# Revit family: CA-4_DWDI_ARR_3_CW_UBD
name_source: partatom
category: Mechanical Equipment
units: mm (PartAtom-declared; Revit-internal decimal feet)

## family parameters
Always vertical = Yes
Cut with Voids When Loaded = No
Part Type = Normal
Room Calculation Point = No
Round Connector Dimension = Use Radius
Shared = No
Work Plane-Based = No

## types (54) — shared parameters
0 = 0"
1" = 1"
1.5 = 1 1/2"
2" = 2"
2' = 24"
3" = 3"
4" = 4"
Manufacturer = Loren Cook Company
ONE EIGTH = 1/8"
Type Comments = Airfoil Centrifugal Blower Arrangement 3 Clockwise Up Blast Discharge
URL = www.lorencook.com

## per-type parameters (varying)
- 120_CA-4_DWDI_ARR_3_CW_UBD_CLASS_1: (B/2)+.125"=8 31/32"; (B/2)+J=10 27/32"; (F/2)-S=3 7/8"; -(B/2)-J=-10 27/32"; -A=-12 1/8"; -B=-17 11/16"; -B/2=-8 27/32"; -J*1.5=-3"; -L+M=-22 15/16"; A=12 1/8"; A+.25"=12 3/8"; B=17 11/16"; B+.25"=17 15/16"; B/2=8 27/32"; D=25 15/16"; D/2=12 31/32"; D/8=3 1/4"; E=10 3/4"; EE=10 3/4"; F=22 3/4"; F-G=12 3/8"; F/2=11 3/8"; G=10 3/8"; G+(INLET_RAD+1.5")=20"; G+N=11 13/16"; G-(INLET_RAD+1.5")=3/4"; H=2"; INLET_DIA=16 1/4"; INLET_RAD=8 1/8"; INLET_RAD+1.5"=9 5/8"; INLET_RAD/2=4 1/16"; J=2"; J*1.5=3"; J-.125"=1 7/8"; L=28 11/16"; M=5 3/4"; Model=CA-4 DWDI CW UBD Class 1; N=1 7/16"; N*2=2 7/8"; N+A+H=15 9/16"; N/2=23/32"; O=9 31/32"; P=19 15/16"; P/2=9 31/32"; S=7 1/2"; T=11/16"; T/2=11/32"
- 120_CA-4_DWDI_ARR_3_CW_UBD_CLASS_2: (B/2)+.125"=8 31/32"; (B/2)+J=10 27/32"; (F/2)-S=3 7/8"; -(B/2)-J=-10 27/32"; -A=-12 1/8"; -B=-17 11/16"; -B/2=-8 27/32"; -J*1.5=-3"; -L+M=-23 5/16"; A=12 1/8"; A+.25"=12 3/8"; B=17 11/16"; B+.25"=17 15/16"; B/2=8 27/32"; D=25 15/16"; D/2=12 31/32"; D/8=3 1/4"; E=10 3/4"; EE=10 3/4"; F=22 3/4"; F-G=12 3/8"; F/2=11 3/8"; G=10 3/8"; G+(INLET_RAD+1.5")=20"; G+N=12 1/16"; G-(INLET_RAD+1.5")=3/4"; H=2"; INLET_DIA=16 1/4"; INLET_RAD=8 1/8"; INLET_RAD+1.5"=9 5/8"; INLET_RAD/2=4 1/16"; J=2"; J*1.5=3"; J-.125"=1 7/8"; L=29 7/16"; M=6 1/8"; Model=CA-4 DWDI CW UBD Class 2; N=1 11/16"; N*2=3 3/8"; N+A+H=15 13/16"; N/2=27/32"; O=9 31/32"; P=19 15/16"; P/2=9 31/32"; S=7 1/2"; T=11/16"; T/2=11/32"
- 120_CA-4_DWDI_ARR_3_CW_UBD_CLASS_3: (B/2)+.125"=8 31/32"; (B/2)+J=10 27/32"; (F/2)-S=3 7/8"; -(B/2)-J=-10 27/32"; -A=-12 1/8"; -B=-17 11/16"; -B/2=-8 27/32"; -J*1.5=-3"; -L+M=-23 9/16"; A=12 1/8"; A+.25"=12 3/8"; B=17 11/16"; B+.25"=17 15/16"; B/2=8 27/32"; D=25 15/16"; D/2=12 31/32"; D/8=3 1/4"; E=10 3/4"; EE=10 3/4"; F=22 3/4"; F-G=12 3/8"; F/2=11 3/8"; G=10 3/8"; G+(INLET_RAD+1.5")=20"; G+N=12 5/16"; G-(INLET_RAD+1.5")=3/4"; H=2"; INLET_DIA=16 1/4"; INLET_RAD=8 1/8"; INLET_RAD+1.5"=9 5/8"; INLET_RAD/2=4 1/16"; J=2"; J*1.5=3"; J-.125"=1 7/8"; L=29 15/16"; M=6 3/8"; Model=CA-4 DWDI CW UBD Class 3; N=1 15/16"; N*2=3 7/8"; N+A+H=16 1/16"; N/2=31/32"; O=9 31/32"; P=19 15/16"; P/2=9 31/32"; S=7 1/2"; T=11/16"; T/2=11/32"
- 135_CA-4_DWDI_ARR_3_CW_UBD_CLASS_1: (B/2)+.125"=10 3/32"; (B/2)+J=11 31/32"; (F/2)-S=4 1/4"; -(B/2)-J=-11 31/32"; -A=-13 5/8"; -B=-19 15/16"; -B/2=-9 31/32"; -J*1.5=-3"; -L+M=-25 3/16"; A=13 5/8"; A+.25"=13 7/8"; B=19 15/16"; B+.25"=20 3/16"; B/2=9 31/32"; D=25 1/2"; D/2=12 3/4"; D/8=3 3/16"; E=12"; EE=12"; F=25 1/2"; F-G=13 7/8"; F/2=12 3/4"; G=11 5/8"; G+(INLET_RAD+1.5")=22"; G+N=13 1/16"; G-(INLET_RAD+1.5")=1 1/4"; H=2"; INLET_DIA=17 3/4"; INLET_RAD=8 7/8"; INLET_RAD+1.5"=10 3/8"; INLET_RAD/2=4 7/16"; J=2"; J*1.5=3"; J-.125"=1 7/8"; L=30 15/16"; M=5 3/4"; Model=CA-4 DWDI CW UBD Class 1; N=1 7/16"; N*2=2 7/8"; N+A+H=17 1/16"; N/2=23/32"; O=11 3/32"; P=22 3/16"; P/2=11 3/32"; S=8 1/2"; T=11/16"; T/2=11/32"
- 135_CA-4_DWDI_ARR_3_CW_UBD_CLASS_2: (B/2)+.125"=10 3/32"; (B/2)+J=11 31/32"; (F/2)-S=4 1/4"; -(B/2)-J=-11 31/32"; -A=-13 5/8"; -B=-19 15/16"; -B/2=-9 31/32"; -J*1.5=-3"; -L+M=-25 9/16"; A=13 5/8"; A+.25"=13 7/8"; B=19 15/16"; B+.25"=20 3/16"; B/2=9 31/32"; D=28 13/16"; D/2=14 13/32"; D/8=3 19/32"; E=12"; EE=12"; F=25 1/2"; F-G=13 7/8"; F/2=12 3/4"; G=11 5/8"; G+(INLET_RAD+1.5")=22"; G+N=13 5/16"; G-(INLET_RAD+1.5")=1 1/4"; H=2"; INLET_DIA=17 3/4"; INLET_RAD=8 7/8"; INLET_RAD+1.5"=10 3/8"; INLET_RAD/2=4 7/16"; J=2"; J*1.5=3"; J-.125"=1 7/8"; L=31 11/16"; M=6 1/8"; Model=CA-4 DWDI CW UBD Class 2; N=1 11/16"; N*2=3 3/8"; N+A+H=17 5/16"; N/2=27/32"; O=11 3/32"; P=22 3/16"; P/2=11 3/32"; S=8 1/2"; T=11/16"; T/2=11/32"
- 135_CA-4_DWDI_ARR_3_CW_UBD_CLASS_3: (B/2)+.125"=10 3/32"; (B/2)+J=11 31/32"; (F/2)-S=4 1/4"; -(B/2)-J=-11 31/32"; -A=-13 5/8"; -B=-19 15/16"; -B/2=-9 31/32"; -J*1.5=-3"; -L+M=-26 1/16"; A=13 5/8"; A+.25"=13 7/8"; B=19 15/16"; B+.25"=20 3/16"; B/2=9 31/32"; D=28 13/16"; D/2=14 13/32"; D/8=3 19/32"; E=12"; EE=12"; F=25 1/2"; F-G=13 7/8"; F/2=12 3/4"; G=11 5/8"; G+(INLET_RAD+1.5")=22"; G+N=13 13/16"; G-(INLET_RAD+1.5")=1 1/4"; H=2"; INLET_DIA=17 3/4"; INLET_RAD=8 7/8"; INLET_RAD+1.5"=10 3/8"; INLET_RAD/2=4 7/16"; J=2"; J*1.5=3"; J-.125"=1 7/8"; L=32 11/16"; M=6 5/8"; Model=CA-4 DWDI CW UBD Class 3; N=2 3/16"; N*2=4 3/8"; N+A+H=17 13/16"; N/2=1 3/32"; O=11 3/32"; P=22 3/16"; P/2=11 3/32"; S=8 1/2"; T=11/16"; T/2=11/32"
- 150_CA-4_DWDI_ARR_3_CW_UBD_CLASS_1: (B/2)+.125"=11 1/8"; (B/2)+J=13"; (F/2)-S=5 1/16"; -(B/2)-J=-13"; -A=-15 1/4"; -B=-22"; -B/2=-11"; -J*1.5=-3"; -L+M=-27 5/8"; A=15 1/4"; A+.25"=15 1/2"; B=22"; B+.25"=22 1/4"; B/2=11"; D=31 11/16"; D/2=15 27/32"; D/8=3 31/32"; E=13 1/4"; EE=13 1/4"; F=28 1/8"; F-G=15 1/4"; F/2=14 1/16"; G=12 7/8"; G+(INLET_RAD+1.5")=24"; G+N=14 9/16"; G-(INLET_RAD+1.5")=1 3/4"; H=2"; INLET_DIA=19 1/4"; INLET_RAD=9 5/8"; INLET_RAD+1.5"=11 1/8"; INLET_RAD/2=4 13/16"; J=2"; J*1.5=3"; J-.125"=1 7/8"; L=34 1/4"; M=6 5/8"; Model=CA-4 DWDI CW UBD Class 1; N=1 11/16"; N*2=3 3/8"; N+A+H=18 15/16"; N/2=27/32"; O=12 1/8"; P=24 1/4"; P/2=12 1/8"; S=9"; T=11/16"; T/2=11/32"
- 150_CA-4_DWDI_ARR_3_CW_UBD_CLASS_2: (B/2)+.125"=11 1/8"; (B/2)+J=13"; (F/2)-S=5 1/16"; -(B/2)-J=-13"; -A=-15 1/4"; -B=-22"; -B/2=-11"; -J*1.5=-3"; -L+M=-27 7/8"; A=15 1/4"; A+.25"=15 1/2"; B=22"; B+.25"=22 1/4"; B/2=11"; D=31 11/16"; D/2=15 27/32"; D/8=3 31/32"; E=13 1/4"; EE=13 1/4"; F=28 1/8"; F-G=15 1/4"; F/2=14 1/16"; G=12 7/8"; G+(INLET_RAD+1.5")=24"; G+N=14 13/16"; G-(INLET_RAD+1.5")=1 3/4"; H=2"; INLET_DIA=19 1/4"; INLET_RAD=9 5/8"; INLET_RAD+1.5"=11 1/8"; INLET_RAD/2=4 13/16"; J=2"; J*1.5=3"; J-.125"=1 7/8"; L=34 3/4"; M=6 7/8"; Model=CA-4 DWDI CW UBD Class 2; N=1 15/16"; N*2=3 7/8"; N+A+H=19 3/16"; N/2=31/32"; O=12 1/8"; P=24 1/4"; P/2=12 1/8"; S=9"; T=11/16"; T/2=11/32"
- 150_CA-4_DWDI_ARR_3_CW_UBD_CLASS_3: (B/2)+.125"=11 1/8"; (B/2)+J=13"; (F/2)-S=5 1/16"; -(B/2)-J=-13"; -A=-15 1/4"; -B=-22"; -B/2=-11"; -J*1.5=-3"; -L+M=-28 1/4"; A=15 1/4"; A+.25"=15 1/2"; B=22"; B+.25"=22 1/4"; B/2=11"; D=31 11/16"; D/2=15 27/32"; D/8=3 31/32"; E=13 1/4"; EE=13 1/4"; F=28 1/8"; F-G=15 1/4"; F/2=14 1/16"; G=12 7/8"; G+(INLET_RAD+1.5")=24"; G+N=15 5/16"; G-(INLET_RAD+1.5")=1 3/4"; H=2"; INLET_DIA=19 1/4"; INLET_RAD=9 5/8"; INLET_RAD+1.5"=11 1/8"; INLET_RAD/2=4 13/16"; J=2"; J*1.5=3"; J-.125"=1 7/8"; L=35 1/2"; M=7 1/4"; Model=CA-4 DWDI CW UBD Class 3; N=2 7/16"; N*2=4 7/8"; N+A+H=19 11/16"; N/2=1 7/32"; O=12 1/8"; P=24 1/4"; P/2=12 1/8"; S=9"; T=11/16"; T/2=11/32"
- 165_CA-4_DWDI_ARR_3_CW_UBD_CLASS_1: (B/2)+.125"=12 1/8"; (B/2)+J=14"; (F/2)-S=5 7/16"; -(B/2)-J=-14"; -A=-16 15/16"; -B=-24"; -B/2=-12"; -J*1.5=-3"; -L+M=-29 5/8"; A=16 15/16"; A+.25"=17 3/16"; B=24"; B+.25"=24 1/4"; B/2=12"; D=34 7/16"; D/2=17 7/32"; D/8=4 5/16"; E=14 3/8"; EE=14 3/8"; F=30 7/8"; F-G=16 5/8"; F/2=15 7/16"; G=14 1/4"; G+(INLET_RAD+1.5")=26 3/8"; G+N=15 15/16"; G-(INLET_RAD+1.5")=2 1/8"; H=2"; INLET_DIA=21 1/4"; INLET_RAD=10 5/8"; INLET_RAD+1.5"=12 1/8"; INLET_RAD/2=5 5/16"; J=2"; J*1.5=3"; J-.125"=1 7/8"; L=36 1/4"; M=6 5/8"; Model=CA-4 DWDI CW UBD Class 1; N=1 11/16"; N*2=3 3/8"; N+A+H=20 5/8"; N/2=27/32"; O=13 1/8"; P=26 1/4"; P/2=13 1/8"; S=10"; T=11/16"; T/2=11/32"
- 165_CA-4_DWDI_ARR_3_CW_UBD_CLASS_2: (B/2)+.125"=12 1/8"; (B/2)+J=14"; (F/2)-S=5 7/16"; -(B/2)-J=-14"; -A=-16 15/16"; -B=-24"; -B/2=-12"; -J*1.5=-3"; -L+M=-29 7/8"; A=16 15/16"; A+.25"=17 3/16"; B=24"; B+.25"=24 1/4"; B/2=12"; D=34 7/16"; D/2=17 7/32"; D/8=4 5/16"; E=14 3/8"; EE=14 3/8"; F=30 7/8"; F-G=16 5/8"; F/2=15 7/16"; G=14 1/4"; G+(INLET_RAD+1.5")=26 3/8"; G+N=16 3/16"; G-(INLET_RAD+1.5")=2 1/8"; H=2"; INLET_DIA=21 1/4"; INLET_RAD=10 5/8"; INLET_RAD+1.5"=12 1/8"; INLET_RAD/2=5 5/16"; J=2"; J*1.5=3"; J-.125"=1 7/8"; L=36 3/4"; M=6 7/8"; Model=CA-4 DWDI CW UBD Class 2; N=1 15/16"; N*2=3 7/8"; N+A+H=20 7/8"; N/2=31/32"; O=13 1/8"; P=26 1/4"; P/2=13 1/8"; S=10"; T=11/16"; T/2=11/32"
- 165_CA-4_DWDI_ARR_3_CW_UBD_CLASS_3: (B/2)+.125"=12 1/8"; (B/2)+J=14"; (F/2)-S=5 7/16"; -(B/2)-J=-14"; -A=-16 15/16"; -B=-24"; -B/2=-12"; -J*1.5=-3"; -L+M=-30 5/16"; A=16 15/16"; A+.25"=17 3/16"; B=24"; B+.25"=24 1/4"; B/2=12"; D=34 7/16"; D/2=17 7/32"; D/8=4 5/16"; E=14 3/8"; EE=14 3/8"; F=30 7/8"; F-G=16 5/8"; F/2=15 7/16"; G=14 1/4"; G+(INLET_RAD+1.5")=26 3/8"; G+N=16 11/16"; G-(INLET_RAD+1.5")=2 1/8"; H=2"; INLET_DIA=21 1/4"; INLET_RAD=10 5/8"; INLET_RAD+1.5"=12 1/8"; INLET_RAD/2=5 5/16"; J=2"; J*1.5=3"; J-.125"=1 7/8"; L=37 1/2"; M=7 3/16"; Model=CA-4 DWDI CW UBD Class 3; N=2 7/16"; N*2=4 7/8"; N+A+H=21 3/8"; N/2=1 7/32"; O=13 1/8"; P=26 1/4"; P/2=13 1/8"; S=10"; T=11/16"; T/2=11/32"
- 180_CA-4_DWDI_ARR_3_CW_UBD_CLASS_1: (B/2)+.125"=13 5/32"; (B/2)+J=15 1/32"; (F/2)-S=5 13/16"; -(B/2)-J=-15 1/32"; -A=-18 1/2"; -B=-26 1/16"; -B/2=-13 1/32"; -J*1.5=-3"; -L+M=-31 11/16"; A=18 1/2"; A+.25"=18 3/4"; B=26 1/16"; B+.25"=26 5/16"; B/2=13 1/32"; D=37 5/16"; D/2=18 21/32"; D/8=4 21/32"; E=15 5/8"; EE=15 5/8"; F=33 5/8"; F-G=18 1/8"; F/2=16 13/16"; G=15 1/2"; G+(INLET_RAD+1.5")=28 3/8"; G+N=17 3/16"; G-(INLET_RAD+1.5")=2 5/8"; H=2"; INLET_DIA=22 3/4"; INLET_RAD=11 3/8"; INLET_RAD+1.5"=12 7/8"; INLET_RAD/2=5 11/16"; J=2"; J*1.5=3"; J-.125"=1 7/8"; L=38 13/16"; M=7 1/8"; Model=CA-4 DWDI CW UBD Class 1; N=1 11/16"; N*2=3 3/8"; N+A+H=22 3/16"; N/2=27/32"; O=14 5/32"; P=28 5/16"; P/2=14 5/32"; S=11"; T=11/16"; T/2=11/32"
- 180_CA-4_DWDI_ARR_3_CW_UBD_CLASS_2: (B/2)+.125"=13 5/32"; (B/2)+J=15 1/32"; (F/2)-S=5 13/16"; -(B/2)-J=-15 1/32"; -A=-18 1/2"; -B=-26 1/16"; -B/2=-13 1/32"; -J*1.5=-3"; -L+M=-31 15/16"; A=18 1/2"; A+.25"=18 3/4"; B=26 1/16"; B+.25"=26 5/16"; B/2=13 1/32"; D=37 5/16"; D/2=18 21/32"; D/8=4 21/32"; E=15 5/8"; EE=15 5/8"; F=33 5/8"; F-G=18 1/8"; F/2=16 13/16"; G=15 1/2"; G+(INLET_RAD+1.5")=28 3/8"; G+N=17 7/16"; G-(INLET_RAD+1.5")=2 5/8"; H=2"; INLET_DIA=22 3/4"; INLET_RAD=11 3/8"; INLET_RAD+1.5"=12 7/8"; INLET_RAD/2=5 11/16"; J=2"; J*1.5=3"; J-.125"=1 7/8"; L=39 5/16"; M=7 3/8"; Model=CA-4 DWDI CW UBD Class 2; N=1 15/16"; N*2=3 7/8"; N+A+H=22 7/16"; N/2=31/32"; O=14 5/32"; P=28 5/16"; P/2=14 5/32"; S=11"; T=11/16"; T/2=11/32"
- 180_CA-4_DWDI_ARR_3_CW_UBD_CLASS_3: (B/2)+.125"=13 5/32"; (B/2)+J=15 1/32"; (F/2)-S=5 13/16"; -(B/2)-J=-15 1/32"; -A=-18 1/2"; -B=-26 1/16"; -B/2=-13 1/32"; -J*1.5=-3"; -L+M=-32 5/16"; A=18 1/2"; A+.25"=18 3/4"; B=26 1/16"; B+.25"=26 5/16"; B/2=13 1/32"; D=37 5/16"; D/2=18 21/32"; D/8=4 21/32"; E=15 5/8"; EE=15 5/8"; F=33 5/8"; F-G=18 1/8"; F/2=16 13/16"; G=15 1/2"; G+(INLET_RAD+1.5")=28 3/8"; G+N=17 15/16"; G-(INLET_RAD+1.5")=2 5/8"; H=2"; INLET_DIA=22 3/4"; INLET_RAD=11 3/8"; INLET_RAD+1.5"=12 7/8"; INLET_RAD/2=5 11/16"; J=2"; J*1.5=3"; J-.125"=1 7/8"; L=40 1/16"; M=7 3/4"; Model=CA-4 DWDI CW UBD Class 3; N=2 7/16"; N*2=4 7/8"; N+A+H=22 15/16"; N/2=1 7/32"; O=14 5/32"; P=28 5/16"; P/2=14 5/32"; S=11"; T=11/16"; T/2=11/32"
- 195_CA-4_DWDI_ARR_3_CW_UBD_CLASS_1: (B/2)+.125"=14 11/32"; (B/2)+J=16 7/32"; (F/2)-S=6 5/8"; -(B/2)-J=-16 7/32"; -A=-19 1/2"; -B=-28 7/16"; -B/2=-14 7/32"; -J*1.5=-3"; -L+M=-34 7/16"; A=19 1/2"; A+.25"=19 3/4"; B=28 7/16"; B+.25"=28 11/16"; B/2=14 7/32"; D=40 1/16"; D/2=20 1/32"; D/8=5"; E=16 3/4"; EE=16 3/4"; F=36 1/4"; F-G=19 1/2"; F/2=18 1/8"; G=16 3/4"; G+(INLET_RAD+1.5")=30 3/8"; G+N=18 11/16"; G-(INLET_RAD+1.5")=3 1/8"; H=2"; INLET_DIA=24 1/4"; INLET_RAD=12 1/8"; INLET_RAD+1.5"=13 5/8"; INLET_RAD/2=6 1/16"; J=2"; J*1.5=3"; J-.125"=1 7/8"; L=41 11/16"; M=7 1/4"; Model=CA-4 DWDI CW UBD Class 1; N=1 15/16"; N*2=3 7/8"; N+A+H=23 7/16"; N/2=31/32"; O=15 11/32"; P=30 11/16"; P/2=15 11/32"; S=11 1/2"; T=11/16"; T/2=11/32"
- 195_CA-4_DWDI_ARR_3_CW_UBD_CLASS_2: (B/2)+.125"=14 11/32"; (B/2)+J=16 7/32"; (F/2)-S=6 5/8"; -(B/2)-J=-16 7/32"; -A=-19 1/2"; -B=-28 7/16"; -B/2=-14 7/32"; -J*1.5=-3"; -L+M=-34 9/16"; A=19 1/2"; A+.25"=19 3/4"; B=28 7/16"; B+.25"=28 11/16"; B/2=14 7/32"; D=40 1/16"; D/2=20 1/32"; D/8=5"; E=16 3/4"; EE=16 3/4"; F=36 1/4"; F-G=19 1/2"; F/2=18 1/8"; G=16 3/4"; G+(INLET_RAD+1.5")=30 3/8"; G+N=18 15/16"; G-(INLET_RAD+1.5")=3 1/8"; H=2"; INLET_DIA=24 1/4"; INLET_RAD=12 1/8"; INLET_RAD+1.5"=13 5/8"; INLET_RAD/2=6 1/16"; J=2"; J*1.5=3"; J-.125"=1 7/8"; L=42 3/16"; M=7 5/8"; Model=CA-4 DWDI CW UBD Class 2; N=2 3/16"; N*2=4 3/8"; N+A+H=23 11/16"; N/2=1 3/32"; O=15 11/32"; P=30 11/16"; P/2=15 11/32"; S=11 1/2"; T=11/16"; T/2=11/32"
- 195_CA-4_DWDI_ARR_3_CW_UBD_CLASS_3: (B/2)+.125"=14 11/32"; (B/2)+J=16 7/32"; (F/2)-S=6 5/8"; -(B/2)-J=-16 7/32"; -A=-19 1/2"; -B=-28 7/16"; -B/2=-14 7/32"; -J*1.5=-3"; -L+M=-34 15/16"; A=19 1/2"; A+.25"=19 3/4"; B=28 7/16"; B+.25"=28 11/16"; B/2=14 7/32"; D=40 1/16"; D/2=20 1/32"; D/8=5"; E=16 3/4"; EE=16 3/4"; F=36 1/4"; F-G=19 1/2"; F/2=18 1/8"; G=16 3/4"; G+(INLET_RAD+1.5")=30 3/8"; G+N=19 7/16"; G-(INLET_RAD+1.5")=3 1/8"; H=2"; INLET_DIA=24 1/4"; INLET_RAD=12 1/8"; INLET_RAD+1.5"=13 5/8"; INLET_RAD/2=6 1/16"; J=2"; J*1.5=3"; J-.125"=1 7/8"; L=42 15/16"; M=8"; Model=CA-4 DWDI CW UBD Class 3; N=2 11/16"; N*2=5 3/8"; N+A+H=24 3/16"; N/2=1 11/32"; O=15 11/32"; P=30 11/16"; P/2=15 11/32"; S=11 1/2"; T=11/16"; T/2=11/32"
- 210_CA-4_DWDI_ARR_3_CW_UBD_CLASS_1: (B/2)+.125"=15 5/16"; (B/2)+J=17 3/16"; (F/2)-S=7 9/16"; -(B/2)-J=-17 3/16"; -A=-21 5/8"; -B=-30 3/8"; -B/2=-15 3/16"; -J*1.5=-3"; -L+M=-36 1/4"; A=21 5/8"; A+.25"=21 7/8"; B=30 3/8"; B+.25"=30 5/8"; B/2=15 3/16"; D=42 15/16"; D/2=21 15/32"; D/8=5 3/8"; E=18"; EE=18"; F=39 1/8"; F-G=21"; F/2=19 9/16"; G=18 1/8"; G+(INLET_RAD+1.5")=32 5/8"; G+N=20 1/16"; G-(INLET_RAD+1.5")=3 5/8"; H=2"; INLET_DIA=26"; INLET_RAD=13"; INLET_RAD+1.5"=14 1/2"; INLET_RAD/2=6 1/2"; J=2"; J*1.5=3"; J-.125"=1 7/8"; L=44 1/8"; M=7 7/8"; Model=CA-4 DWDI CW UBD Class 1; N=1 15/16"; N*2=3 7/8"; N+A+H=25 9/16"; N/2=31/32"; O=6 5/16"; P=32 5/8"; P/2=16 5/16"; S=12"; T=15/16"; T/2=15/32"
- 210_CA-4_DWDI_ARR_3_CW_UBD_CLASS_2: (B/2)+.125"=15 5/16"; (B/2)+J=17 3/16"; (F/2)-S=7 9/16"; -(B/2)-J=-17 3/16"; -A=-21 5/8"; -B=-30 3/8"; -B/2=-15 3/16"; -J*1.5=-3"; -L+M=-36 1/2"; A=21 5/8"; A+.25"=21 7/8"; B=30 3/8"; B+.25"=30 5/8"; B/2=15 3/16"; D=42 15/16"; D/2=21 15/32"; D/8=5 3/8"; E=18"; EE=18"; F=39 1/8"; F-G=21"; F/2=19 9/16"; G=18 1/8"; G+(INLET_RAD+1.5")=32 5/8"; G+N=20 5/16"; G-(INLET_RAD+1.5")=3 5/8"; H=2"; INLET_DIA=26"; INLET_RAD=13"; INLET_RAD+1.5"=14 1/2"; INLET_RAD/2=6 1/2"; J=2"; J*1.5=3"; J-.125"=1 7/8"; L=44 5/8"; M=8 1/8"; Model=CA-4 DWDI CW UBD Class 2; N=2 3/16"; N*2=4 3/8"; N+A+H=25 13/16"; N/2=1 3/32"; O=6 5/16"; P=32 5/8"; P/2=16 5/16"; S=12"; T=15/16"; T/2=15/32"
- 210_CA-4_DWDI_ARR_3_CW_UBD_CLASS_3: (B/2)+.125"=15 5/16"; (B/2)+J=17 3/16"; (F/2)-S=7 9/16"; -(B/2)-J=-17 3/16"; -A=-21 5/8"; -B=-30 3/8"; -B/2=-15 3/16"; -J*1.5=-3"; -L+M=-36 7/8"; A=21 5/8"; A+.25"=21 7/8"; B=30 3/8"; B+.25"=30 5/8"; B/2=15 3/16"; D=42 15/16"; D/2=21 15/32"; D/8=5 3/8"; E=18"; EE=18"; F=39 1/8"; F-G=21"; F/2=19 9/16"; G=18 1/8"; G+(INLET_RAD+1.5")=32 5/8"; G+N=20 13/16"; G-(INLET_RAD+1.5")=3 5/8"; H=2"; INLET_DIA=26"; INLET_RAD=13"; INLET_RAD+1.5"=14 1/2"; INLET_RAD/2=6 1/2"; J=2"; J*1.5=3"; J-.125"=1 7/8"; L=45 3/8"; M=8 1/2"; Model=CA-4 DWDI CW UBD Class 3; N=2 11/16"; N*2=5 3/8"; N+A+H=26 5/16"; N/2=1 11/32"; O=6 5/16"; P=32 5/8"; P/2=16 5/16"; S=12"; T=15/16"; T/2=15/32"
- 225_CA-4_DWDI_ARR_3_CW_UBD_CLASS_1: (B/2)+.125"=16 3/8"; (B/2)+J=18 1/4"; (F/2)-S=8 3/8"; -(B/2)-J=-18 1/4"; -A=-23 3/16"; -B=-32 1/2"; -B/2=-16 1/4"; -J*1.5=-3"; -L+M=-38 3/8"; A=23 3/16"; A+.25"=23 7/16"; B=32 1/2"; B+.25"=32 3/4"; B/2=16 1/4"; D=45 13/16"; D/2=22 29/32"; D/8=5 23/32"; E=19 1/4"; EE=19 1/4"; F=41 3/4"; F-G=22 3/8"; F/2=20 7/8"; G=19 3/8"; G+(INLET_RAD+1.5")=34 5/8"; G+N=21 5/16"; G-(INLET_RAD+1.5")=4 1/8"; H=2"; INLET_DIA=27 1/2"; INLET_RAD=13 3/4"; INLET_RAD+1.5"=15 1/4"; INLET_RAD/2=6 7/8"; J=2"; J*1.5=3"; J-.125"=1 7/8"; L=46 1/4"; M=7 7/8"; Model=CA-4 DWDI CW UBD Class 1; N=1 15/16"; N*2=3 7/8"; N+A+H=27 1/8"; N/2=31/32"; O=17 3/8"; P=34 3/4"; P/2=17 3/8"; S=12 1/2"; T=15/16"; T/2=15/32"
- 225_CA-4_DWDI_ARR_3_CW_UBD_CLASS_2: (B/2)+.125"=16 3/8"; (B/2)+J=18 1/4"; (F/2)-S=8 3/8"; -(B/2)-J=-18 1/4"; -A=-23 3/16"; -B=-32 1/2"; -B/2=-16 1/4"; -J*1.5=-3"; -L+M=-38 3/4"; A=23 3/16"; A+.25"=23 7/16"; B=32 1/2"; B+.25"=32 3/4"; B/2=16 1/4"; D=45 13/16"; D/2=22 29/32"; D/8=5 23/32"; E=19 1/4"; EE=19 1/4"; F=41 3/4"; F-G=22 3/8"; F/2=20 7/8"; G=19 3/8"; G+(INLET_RAD+1.5")=34 5/8"; G+N=21 13/16"; G-(INLET_RAD+1.5")=4 1/8"; H=2"; INLET_DIA=27 1/2"; INLET_RAD=13 3/4"; INLET_RAD+1.5"=15 1/4"; INLET_RAD/2=6 7/8"; J=2"; J*1.5=3"; J-.125"=1 7/8"; L=47"; M=8 1/4"; Model=CA-4 DWDI CW UBD Class 2; N=2 7/16"; N*2=4 7/8"; N+A+H=27 5/8"; N/2=1 7/32"; O=17 3/8"; P=34 3/4"; P/2=17 3/8"; S=12 1/2"; T=15/16"; T/2=15/32"
- 225_CA-4_DWDI_ARR_3_CW_UBD_CLASS_3: (B/2)+.125"=16 3/8"; (B/2)+J=18 1/4"; (F/2)-S=8 3/8"; -(B/2)-J=-18 1/4"; -A=-23 3/16"; -B=-32 1/2"; -B/2=-16 1/4"; -J*1.5=-3"; -L+M=-39"; A=23 3/16"; A+.25"=23 7/16"; B=32 1/2"; B+.25"=32 3/4"; B/2=16 1/4"; D=45 13/16"; D/2=22 29/32"; D/8=5 23/32"; E=19 1/4"; EE=19 1/4"; F=41 3/4"; F-G=22 3/8"; F/2=20 7/8"; G=19 3/8"; G+(INLET_RAD+1.5")=34 5/8"; G+N=22 5/16"; G-(INLET_RAD+1.5")=4 1/8"; H=2"; INLET_DIA=27 1/2"; INLET_RAD=13 3/4"; INLET_RAD+1.5"=15 1/4"; INLET_RAD/2=6 7/8"; J=2"; J*1.5=3"; J-.125"=1 7/8"; L=47 1/2"; M=8 1/2"; Model=CA-4 DWDI CW UBD Class 3; N=2 15/16"; N*2=5 7/8"; N+A+H=28 1/8"; N/2=1 15/32"; O=17 3/8"; P=34 3/4"; P/2=17 3/8"; S=12 1/2"; T=15/16"; T/2=15/32"
- 245_CA-4_DWDI_ARR_3_CW_UBD_CLASS_1: (B/2)+.125"=17 21/32"; (B/2)+J=19 17/32"; (F/2)-S=10 3/16"; -(B/2)-J=-19 17/32"; -A=-25 1/2"; -B=-35 1/16"; -B/2=-17 17/32"; -J*1.5=-3"; -L+M=-41 3/16"; A=25 1/2"; A+.25"=25 3/4"; B=35 1/16"; B+.25"=35 5/16"; B/2=17 17/32"; D=49 5/8"; D/2=24 13/16"; D/8=6 7/32"; E=20 7/8"; EE=20 7/8"; F=45 3/8"; F-G=24 1/4"; F/2=22 11/16"; G=21 1/8"; G+(INLET_RAD+1.5")=37 3/8"; G+N=23 5/16"; G-(INLET_RAD+1.5")=4 7/8"; H=2"; INLET_DIA=29 1/2"; INLET_RAD=14 3/4"; INLET_RAD+1.5"=16 1/4"; INLET_RAD/2=7 3/8"; J=2"; J*1.5=3"; J-.125"=1 7/8"; L=49 13/16"; M=8 5/8"; Model=CA-4 DWDI CW UBD Class 1; N=2 3/16"; N*2=4 3/8"; N+A+H=29 11/16"; N/2=1 3/32"; O=18 21/32"; P=37 5/16"; P/2=18 21/32"; S=12 1/2"; T=15/16"; T/2=15/32"
- 245_CA-4_DWDI_ARR_3_CW_UBD_CLASS_2: (B/2)+.125"=17 21/32"; (B/2)+J=19 17/32"; (F/2)-S=10 3/16"; -(B/2)-J=-19 17/32"; -A=-25 1/2"; -B=-35 1/16"; -B/2=-17 17/32"; -J*1.5=-3"; -L+M=-41 5/16"; A=25 1/2"; A+.25"=25 3/4"; B=35 1/16"; B+.25"=35 5/16"; B/2=17 17/32"; D=49 5/8"; D/2=24 13/16"; D/8=6 7/32"; E=20 7/8"; EE=20 7/8"; F=45 3/8"; F-G=24 1/4"; F/2=22 11/16"; G=21 1/8"; G+(INLET_RAD+1.5")=37 3/8"; G+N=23 9/16"; G-(INLET_RAD+1.5")=4 7/8"; H=2"; INLET_DIA=29 1/2"; INLET_RAD=14 3/4"; INLET_RAD+1.5"=16 1/4"; INLET_RAD/2=7 3/8"; J=2"; J*1.5=3"; J-.125"=1 7/8"; L=50 1/16"; M=8 3/4"; Model=CA-4 DWDI CW UBD Class 2; N=2 7/16"; N*2=4 7/8"; N+A+H=29 15/16"; N/2=1 7/32"; O=18 21/32"; P=37 5/16"; P/2=18 21/32"; S=12 1/2"; T=15/16"; T/2=15/32"
- 245_CA-4_DWDI_ARR_3_CW_UBD_CLASS_3: (B/2)+.125"=17 21/32"; (B/2)+J=19 17/32"; (F/2)-S=10 3/16"; -(B/2)-J=-19 17/32"; -A=-25 1/2"; -B=-35 1/16"; -B/2=-17 17/32"; -J*1.5=-3"; -L+M=-41 15/16"; A=25 1/2"; A+.25"=25 3/4"; B=35 1/16"; B+.25"=35 5/16"; B/2=17 17/32"; D=49 5/8"; D/2=24 13/16"; D/8=6 7/32"; E=20 7/8"; EE=20 7/8"; F=45 3/8"; F-G=24 1/4"; F/2=22 11/16"; G=21 1/8"; G+(INLET_RAD+1.5")=37 3/8"; G+N=23 5/16"; G-(INLET_RAD+1.5")=4 7/8"; H=2"; INLET_DIA=29 1/2"; INLET_RAD=14 3/4"; INLET_RAD+1.5"=16 1/4"; INLET_RAD/2=7 3/8"; J=2"; J*1.5=3"; J-.125"=1 7/8"; L=50 11/16"; M=8 3/4"; Model=CA-4 DWDI CW UBD Class 3; N=2 3/16"; N*2=4 3/8"; N+A+H=29 11/16"; N/2=1 3/32"; O=18 21/32"; P=37 5/16"; P/2=18 21/32"; S=12 1/2"; T=15/16"; T/2=15/32"
- 270_CA-4_DWDI_ARR_3_CW_UBD_CLASS_1: (B/2)+.125"=19 27/32"; (B/2)+J=21 23/32"; (F/2)-S=9 15/16"; -(B/2)-J=-21 23/32"; -A=-27 1/2"; -B=-39 7/16"; -B/2=-19 23/32"; -J*1.5=-3"; -L+M=-45 9/16"; A=27 1/2"; A+.25"=27 3/4"; B=39 7/16"; B+.25"=39 11/16"; B/2=19 23/32"; D=54 7/8"; D/2=27 7/16"; D/8=6 7/8"; E=23 3/8"; EE=23 3/8"; F=49 7/8"; F-G=26 5/8"; F/2=24 15/16"; G=23 1/4"; G+(INLET_RAD+1.5")=40 3/4"; G+N=25 7/16"; G-(INLET_RAD+1.5")=5 3/4"; H=2"; INLET_DIA=32"; INLET_RAD=16"; INLET_RAD+1.5"=17 1/2"; INLET_RAD/2=8"; J=2"; J*1.5=3"; J-.125"=1 7/8"; L=54 3/16"; M=8 5/8"; Model=CA-4 DWDI CW UBD Class 1; N=2 3/16"; N*2=4 3/8"; N+A+H=31 11/16"; N/2=1 3/32"; O=20 27/32"; P=41 11/16"; P/2=20 27/32"; S=15"; T=15/16"; T/2=15/32"
- 270_CA-4_DWDI_ARR_3_CW_UBD_CLASS_2: (B/2)+.125"=19 27/32"; (B/2)+J=21 23/32"; (F/2)-S=9 15/16"; -(B/2)-J=-21 23/32"; -A=-27 1/2"; -B=-39 7/16"; -B/2=-19 23/32"; -J*1.5=-3"; -L+M=-45 15/16"; A=27 1/2"; A+.25"=27 3/4"; B=39 7/16"; B+.25"=39 11/16"; B/2=19 23/32"; D=54 7/8"; D/2=27 7/16"; D/8=6 7/8"; E=23 3/8"; EE=23 3/8"; F=49 7/8"; F-G=26 5/8"; F/2=24 15/16"; G=23 1/4"; G+(INLET_RAD+1.5")=40 3/4"; G+N=25 15/16"; G-(INLET_RAD+1.5")=5 3/4"; H=2"; INLET_DIA=32"; INLET_RAD=16"; INLET_RAD+1.5"=17 1/2"; INLET_RAD/2=8"; J=2"; J*1.5=3"; J-.125"=1 7/8"; L=54 15/16"; M=9"; Model=CA-4 DWDI CW UBD Class 2; N=2 11/16"; N*2=5 3/8"; N+A+H=32 3/16"; N/2=1 11/32"; O=20 27/32"; P=41 11/16"; P/2=20 27/32"; S=15"; T=15/16"; T/2=15/32"
- 270_CA-4_DWDI_ARR_3_CW_UBD_CLASS_3: (B/2)+.125"=19 27/32"; (B/2)+J=21 23/32"; (F/2)-S=9 15/16"; -(B/2)-J=-21 23/32"; -A=-27 1/2"; -B=-39 7/16"; -B/2=-19 23/32"; -J*1.5=-3"; -L+M=-46 5/16"; A=27 1/2"; A+.25"=27 3/4"; B=39 7/16"; B+.25"=39 11/16"; B/2=19 23/32"; D=54 7/8"; D/2=27 7/16"; D/8=6 7/8"; E=23 3/8"; EE=23 3/8"; F=49 7/8"; F-G=26 5/8"; F/2=24 15/16"; G=23 1/4"; G+(INLET_RAD+1.5")=40 3/4"; G+N=25 7/16"; G-(INLET_RAD+1.5")=5 3/4"; H=2"; INLET_DIA=32"; INLET_RAD=16"; INLET_RAD+1.5"=17 1/2"; INLET_RAD/2=8"; J=2"; J*1.5=3"; J-.125"=1 7/8"; L=55 1/16"; M=8 3/4"; Model=CA-4 DWDI CW UBD Class 3; N=2 3/16"; N*2=4 3/8"; N+A+H=31 11/16"; N/2=1 3/32"; O=20 27/32"; P=41 11/16"; P/2=20 27/32"; S=15"; T=15/16"; T/2=15/32"
- 300_CA-4_DWDI_ARR_3_CW_UBD_CLASS_1: (B/2)+.125"=21 5/8"; (B/2)+J=23 1/2"; (F/2)-S=11 3/16"; -(B/2)-J=-23 1/2"; -A=-31 3/16"; -B=-43"; -B/2=-21 1/2"; -J*1.5=-3"; -L+M=-49 1/4"; A=31 3/16"; A+.25"=31 7/16"; B=43"; B+.25"=43 1/4"; B/2=21 1/2"; D=60 1/8"; D/2=30 1/16"; D/8=7 17/32"; E=25 3/8"; EE=25 3/8"; F=55 3/8"; F-G=29 1/2"; F/2=27 11/16"; G=25 7/8"; G+(INLET_RAD+1.5")=44 7/8"; G+N=28 5/16"; G-(INLET_RAD+1.5")=6 7/8"; H=2"; INLET_DIA=35"; INLET_RAD=17 1/2"; INLET_RAD+1.5"=19"; INLET_RAD/2=8 3/4"; J=2"; J*1.5=3"; J-.125"=1 7/8"; L=58 1/2"; M=9 1/4"; Model=CA-4 DWDI CW UBD Class 1; N=2 7/16"; N*2=4 7/8"; N+A+H=35 5/8"; N/2=1 7/32"; O=22 5/8"; P=45 1/4"; P/2=22 5/8"; S=16 1/2"; T=15/16"; T/2=15/32"
- 300_CA-4_DWDI_ARR_3_CW_UBD_CLASS_2: (B/2)+.125"=21 5/8"; (B/2)+J=23 1/2"; (F/2)-S=11 3/16"; -(B/2)-J=-23 1/2"; -A=-31 3/16"; -B=-43"; -B/2=-21 1/2"; -J*1.5=-3"; -L+M=-49 1/2"; A=31 3/16"; A+.25"=31 7/16"; B=43"; B+.25"=43 1/4"; B/2=21 1/2"; D=60 1/8"; D/2=30 1/16"; D/8=7 17/32"; E=25 3/8"; EE=25 3/8"; F=55 3/8"; F-G=29 1/2"; F/2=27 11/16"; G=25 7/8"; G+(INLET_RAD+1.5")=44 7/8"; G+N=28 9/16"; G-(INLET_RAD+1.5")=6 7/8"; H=2"; INLET_DIA=35"; INLET_RAD=17 1/2"; INLET_RAD+1.5"=19"; INLET_RAD/2=8 3/4"; J=2"; J*1.5=3"; J-.125"=1 7/8"; L=59"; M=9 1/2"; Model=CA-4 DWDI CW UBD Class 2; N=2 11/16"; N*2=5 3/8"; N+A+H=35 7/8"; N/2=1 11/32"; O=22 5/8"; P=45 1/4"; P/2=22 5/8"; S=16 1/2"; T=15/16"; T/2=15/32"
- 300_CA-4_DWDI_ARR_3_CW_UBD_CLASS_3: (B/2)+.125"=21 5/8"; (B/2)+J=23 1/2"; (F/2)-S=11 3/16"; -(B/2)-J=-23 1/2"; -A=-31 3/16"; -B=-43"; -B/2=-21 1/2"; -J*1.5=-3"; -L+M=-49 7/8"; A=31 3/16"; A+.25"=31 7/16"; B=43"; B+.25"=43 1/4"; B/2=21 1/2"; D=60 1/8"; D/2=30 1/16"; D/8=7 17/32"; E=25 3/8"; EE=25 3/8"; F=55 3/8"; F-G=29 1/2"; F/2=27 11/16"; G=25 7/8"; G+(INLET_RAD+1.5")=44 7/8"; G+N=28 5/16"; G-(INLET_RAD+1.5")=6 7/8"; H=2"; INLET_DIA=35"; INLET_RAD=17 1/2"; INLET_RAD+1.5"=19"; INLET_RAD/2=8 3/4"; J=2"; J*1.5=3"; J-.125"=1 7/8"; L=59 3/8"; M=9 1/2"; Model=CA-4 DWDI CW UBD Class 3; N=2 7/16"; N*2=4 7/8"; N+A+H=35 5/8"; N/2=1 7/32"; O=22 5/8"; P=45 1/4"; P/2=22 5/8"; S=16 1/2"; T=15/16"; T/2=15/32"
- 330_CA-4_DWDI_ARR_3_CW_UBD_CLASS_1: (B/2)+.125"=23 21/32"; (B/2)+J=25 17/32"; (F/2)-S=12 3/8"; -(B/2)-J=-25 17/32"; -A=-34 1/2"; -B=-47 1/16"; -B/2=-23 17/32"; -J*1.5=-3"; -L+M=-53 1/2"; A=34 1/2"; A+.25"=34 3/4"; B=47 1/16"; B+.25"=47 5/16"; B/2=23 17/32"; D=65 15/16"; D/2=32 31/32"; D/8=8 1/4"; E=27 7/8"; EE=27 7/8"; F=60 3/4"; F-G=32 3/8"; F/2=30 3/8"; G=28 3/8"; G+(INLET_RAD+1.5")=48 7/8"; G+N=31 1/16"; G-(INLET_RAD+1.5")=7 7/8"; H=2"; INLET_DIA=38"; INLET_RAD=19"; INLET_RAD+1.5"=20 1/2"; INLET_RAD/2=9 1/2"; J=2"; J*1.5=3"; J-.125"=1 7/8"; L=63 9/16"; M=10 1/16"; Model=CA-4 DWDI CW UBD Class 1; N=2 11/16"; N*2=5 3/8"; N+A+H=39 3/16"; N/2=1 11/32"; O=24 21/32"; P=49 5/16"; P/2=24 21/32"; S=18"; T=15/16"; T/2=15/32"
- 330_CA-4_DWDI_ARR_3_CW_UBD_CLASS_2: (B/2)+.125"=23 21/32"; (B/2)+J=25 17/32"; (F/2)-S=12 3/8"; -(B/2)-J=-25 17/32"; -A=-34 1/2"; -B=-47 1/16"; -B/2=-23 17/32"; -J*1.5=-3"; -L+M=-54 1/16"; A=34 1/2"; A+.25"=34 3/4"; B=47 1/16"; B+.25"=47 5/16"; B/2=23 17/32"; D=65 15/16"; D/2=32 31/32"; D/8=8 1/4"; E=27 7/8"; EE=27 7/8"; F=60 3/4"; F-G=32 3/8"; F/2=30 3/8"; G=28 3/8"; G+(INLET_RAD+1.5")=48 7/8"; G+N=30 9/16"; G-(INLET_RAD+1.5")=7 7/8"; H=2"; INLET_DIA=38"; INLET_RAD=19"; INLET_RAD+1.5"=20 1/2"; INLET_RAD/2=9 1/2"; J=2"; J*1.5=3"; J-.125"=1 7/8"; L=63 11/16"; M=9 5/8"; Model=CA-4 DWDI CW UBD Class 2; N=2 3/16"; N*2=4 3/8"; N+A+H=38 11/16"; N/2=1 3/32"; O=24 21/32"; P=49 5/16"; P/2=24 21/32"; S=18"; T=15/16"; T/2=15/32"
- 330_CA-4_DWDI_ARR_3_CW_UBD_CLASS_3: (B/2)+.125"=23 21/32"; (B/2)+J=25 17/32"; (F/2)-S=12 3/8"; -(B/2)-J=-25 17/32"; -A=-34 1/2"; -B=-47 1/16"; -B/2=-23 17/32"; -J*1.5=-3"; -L+M=-53 15/16"; A=34 1/2"; A+.25"=34 3/4"; B=47 1/16"; B+.25"=47 5/16"; B/2=23 17/32"; D=65 15/16"; D/2=32 31/32"; D/8=8 1/4"; E=27 7/8"; EE=27 7/8"; F=60 3/4"; F-G=32 3/8"; F/2=30 3/8"; G=28 3/8"; G+(INLET_RAD+1.5")=48 7/8"; G+N=30 13/16"; G-(INLET_RAD+1.5")=7 7/8"; H=2"; INLET_DIA=38"; INLET_RAD=19"; INLET_RAD+1.5"=20 1/2"; INLET_RAD/2=9 1/2"; J=2"; J*1.5=3"; J-.125"=1 7/8"; L=63 15/16"; M=10"; Model=CA-4 DWDI CW UBD Class 3; N=2 7/16"; N*2=4 7/8"; N+A+H=38 15/16"; N/2=1 7/32"; O=24 21/32"; P=49 5/16"; P/2=24 21/32"; S=18"; T=15/16"; T/2=15/32"
- 365_CA-4_DWDI_ARR_3_CW_UBD_CLASS_1: (B/2)+.125"=26 7/32"; (B/2)+J=28 3/32"; (F/2)-S=13 1/2"; -(B/2)-J=-28 3/32"; -A=-38 11/16"; -B=-52 3/16"; -B/2=-26 3/32"; -J*1.5=-3"; -L+M=-59"; A=38 11/16"; A+.25"=38 15/16"; B=52 3/16"; B+.25"=52 7/16"; B/2=26 3/32"; D=72 1/2"; D/2=36 1/4"; D/8=9 1/16"; E=30 5/8"; EE=30 5/8"; F=67"; F-G=35 5/8"; F/2=33 1/2"; G=31 3/8"; G+(INLET_RAD+1.5")=53 5/8"; G+N=33 9/16"; G-(INLET_RAD+1.5")=9 1/8"; H=2"; INLET_DIA=41 1/2"; INLET_RAD=20 3/4"; INLET_RAD+1.5"=22 1/4"; INLET_RAD/2=10 3/8"; J=2"; J*1.5=3"; J-.125"=1 7/8"; L=69 5/16"; M=10 5/16"; Model=CA-4 DWDI CW UBD Class 1; N=2 3/16"; N*2=4 3/8"; N+A+H=42 7/8"; N/2=1 3/32"; O=27 7/32"; P=54 7/16"; P/2=27 7/32"; S=20"; T=15/16"; T/2=15/32"
- 365_CA-4_DWDI_ARR_3_CW_UBD_CLASS_2: (B/2)+.125"=26 7/32"; (B/2)+J=28 3/32"; (F/2)-S=13 1/2"; -(B/2)-J=-28 3/32"; -A=-38 11/16"; -B=-52 3/16"; -B/2=-26 3/32"; -J*1.5=-3"; -L+M=-59 1/16"; A=38 11/16"; A+.25"=38 15/16"; B=52 3/16"; B+.25"=52 7/16"; B/2=26 3/32"; D=72 1/2"; D/2=36 1/4"; D/8=9 1/16"; E=30 5/8"; EE=30 5/8"; F=67"; F-G=35 5/8"; F/2=33 1/2"; G=31 3/8"; G+(INLET_RAD+1.5")=53 5/8"; G+N=33 13/16"; G-(INLET_RAD+1.5")=9 1/8"; H=2"; INLET_DIA=41 1/2"; INLET_RAD=20 3/4"; INLET_RAD+1.5"=22 1/4"; INLET_RAD/2=10 3/8"; J=2"; J*1.5=3"; J-.125"=1 7/8"; L=69 9/16"; M=10 1/2"; Model=CA-4 DWDI CW UBD Class 2; N=2 7/16"; N*2=4 7/8"; N+A+H=43 1/8"; N/2=1 7/32"; O=27 7/32"; P=54 7/16"; P/2=27 7/32"; S=20"; T=15/16"; T/2=15/32"
- 365_CA-4_DWDI_ARR_3_CW_UBD_CLASS_3: (B/2)+.125"=26 7/32"; (B/2)+J=28 3/32"; (F/2)-S=13 1/2"; -(B/2)-J=-28 3/32"; -A=-38 11/16"; -B=-52 3/16"; -B/2=-26 3/32"; -J*1.5=-3"; -L+M=-59 9/16"; A=38 11/16"; A+.25"=38 15/16"; B=52 3/16"; B+.25"=52 7/16"; B/2=26 3/32"; D=72 1/2"; D/2=36 1/4"; D/8=9 1/16"; E=30 5/8"; EE=30 5/8"; F=67"; F-G=35 5/8"; F/2=33 1/2"; G=31 3/8"; G+(INLET_RAD+1.5")=53 5/8"; G+N=34 1/16"; G-(INLET_RAD+1.5")=9 1/8"; H=2"; INLET_DIA=41 1/2"; INLET_RAD=20 3/4"; INLET_RAD+1.5"=22 1/4"; INLET_RAD/2=10 3/8"; J=2"; J*1.5=3"; J-.125"=1 7/8"; L=70 1/16"; M=10 1/2"; Model=CA-4 DWDI CW UBD Class 3; N=2 11/16"; N*2=5 3/8"; N+A+H=43 3/8"; N/2=1 11/32"; O=27 7/32"; P=54 7/16"; P/2=27 7/32"; S=20"; T=15/16"; T/2=15/32"
- 402_CA-4_DWDI_ARR_3_CW_UBD_CLASS_1: (B/2)+.125"=29 1/32"; (B/2)+J=31 29/32"; (F/2)-S=14 15/16"; -(B/2)-J=-31 29/32"; -A=-41 3/4"; -B=-57 13/16"; -B/2=-28 29/32"; -J*1.5=-4 1/2"; -L+M=-65 11/16"; A=41 3/4"; A+.25"=42"; B=57 13/16"; B+.25"=58 1/16"; B/2=28 29/32"; D=80 9/16"; D/2=40 9/32"; D/8=10 1/16"; E=33 5/8"; EE=33 5/8"; F=73 7/8"; F-G=39 1/4"; F/2=36 15/16"; G=34 5/8"; G+(INLET_RAD+1.5")=58 3/4"; G+N=37 1/16"; G-(INLET_RAD+1.5")=10 1/2"; H=3"; INLET_DIA=45 1/4"; INLET_RAD=22 5/8"; INLET_RAD+1.5"=24 1/8"; INLET_RAD/2=11 5/16"; J=3"; J*1.5=4 1/2"; J-.125"=2 7/8"; L=75 11/16"; M=10"; Model=CA-4 DWDI CW UBD Class 1; N=2 7/16"; N*2=4 7/8"; N+A+H=47 3/16"; N/2=1 7/32"; O=30 21/32"; P=61 5/16"; P/2=30 21/32"; S=22"; T=1 1/16"; T/2=17/32"
- 402_CA-4_DWDI_ARR_3_CW_UBD_CLASS_2: (B/2)+.125"=29 1/32"; (B/2)+J=31 29/32"; (F/2)-S=14 15/16"; -(B/2)-J=-31 29/32"; -A=-41 3/4"; -B=-57 13/16"; -B/2=-28 29/32"; -J*1.5=-4 1/2"; -L+M=-65 11/16"; A=41 3/4"; A+.25"=42"; B=57 13/16"; B+.25"=58 1/16"; B/2=28 29/32"; D=80 9/16"; D/2=40 9/32"; D/8=10 1/16"; E=33 5/8"; EE=33 5/8"; F=73 7/8"; F-G=39 1/4"; F/2=36 15/16"; G=34 5/8"; G+(INLET_RAD+1.5")=58 3/4"; G+N=37 1/16"; G-(INLET_RAD+1.5")=10 1/2"; H=3"; INLET_DIA=45 1/4"; INLET_RAD=22 5/8"; INLET_RAD+1.5"=24 1/8"; INLET_RAD/2=11 5/16"; J=3"; J*1.5=4 1/2"; J-.125"=2 7/8"; L=75 11/16"; M=10"; Model=CA-4 DWDI CW UBD Class 2; N=2 7/16"; N*2=4 7/8"; N+A+H=47 3/16"; N/2=1 7/32"; O=30 21/32"; P=61 5/16"; P/2=30 21/32"; S=22"; T=1 1/16"; T/2=17/32"
- 402_CA-4_DWDI_ARR_3_CW_UBD_CLASS_3: (B/2)+.125"=29 1/32"; (B/2)+J=31 29/32"; (F/2)-S=14 15/16"; -(B/2)-J=-31 29/32"; -A=-41 3/4"; -B=-57 13/16"; -B/2=-28 29/32"; -J*1.5=-4 1/2"; -L+M=-65 11/16"; A=41 3/4"; A+.25"=42"; B=57 13/16"; B+.25"=58 1/16"; B/2=28 29/32"; D=80 9/16"; D/2=40 9/32"; D/8=10 1/16"; E=33 5/8"; EE=33 5/8"; F=73 7/8"; F-G=39 1/4"; F/2=36 15/16"; G=34 5/8"; G+(INLET_RAD+1.5")=58 3/4"; G+N=37 5/16"; G-(INLET_RAD+1.5")=10 1/2"; H=3"; INLET_DIA=45 1/4"; INLET_RAD=22 5/8"; INLET_RAD+1.5"=24 1/8"; INLET_RAD/2=11 5/16"; J=3"; J*1.5=4 1/2"; J-.125"=2 7/8"; L=76 3/16"; M=10 1/2"; Model=CA-4 DWDI CW UBD Class 3; N=2 11/16"; N*2=5 3/8"; N+A+H=47 7/16"; N/2=1 11/32"; O=30 21/32"; P=61 5/16"; P/2=30 21/32"; S=22"; T=1 1/16"; T/2=17/32"
- 445_CA-4_DWDI_ARR_3_CW_UBD_CLASS_1: (B/2)+.125"=32 1/4"; (B/2)+J=35 1/8"; (F/2)-S=16 3/4"; -(B/2)-J=-35 1/8"; -A=-45 15/16"; -B=-64 1/4"; -B/2=-32 1/8"; -J*1.5=-4 1/2"; -L+M=-72"; A=45 15/16"; A+.25"=46 3/16"; B=64 1/4"; B+.25"=64 1/2"; B/2=32 1/8"; D=88 11/16"; D/2=44 11/32"; D/8=11 3/32"; E=37 1/8"; EE=37 1/8"; F=81 1/2"; F-G=43 1/4"; F/2=40 3/4"; G=38 1/4"; G+(INLET_RAD+1.5")=64 1/2"; G+N=40 11/16"; G-(INLET_RAD+1.5")=12"; H=3"; INLET_DIA=49 1/2"; INLET_RAD=24 3/4"; INLET_RAD+1.5"=26 1/4"; INLET_RAD/2=12 3/8"; J=3"; J*1.5=4 1/2"; J-.125"=2 7/8"; L=82 5/8"; M=10 5/8"; Model=CA-4 DWDI CW UBD Class 1; N=2 7/16"; N*2=4 7/8"; N+A+H=51 3/8"; N/2=1 7/32"; O=33 7/8"; P=67 3/4"; P/2=33 7/8"; S=24"; T=1 1/16"; T/2=17/32"
- 445_CA-4_DWDI_ARR_3_CW_UBD_CLASS_2: (B/2)+.125"=32 1/4"; (B/2)+J=35 1/8"; (F/2)-S=16 3/4"; -(B/2)-J=-35 1/8"; -A=-45 15/16"; -B=-64 1/4"; -B/2=-32 1/8"; -J*1.5=-4 1/2"; -L+M=-72 1/2"; A=45 15/16"; A+.25"=46 3/16"; B=64 1/4"; B+.25"=64 1/2"; B/2=32 1/8"; D=88 11/16"; D/2=44 11/32"; D/8=11 3/32"; E=37 1/8"; EE=37 1/8"; F=81 1/2"; F-G=43 1/4"; F/2=40 3/4"; G=38 1/4"; G+(INLET_RAD+1.5")=64 1/2"; G+N=40 15/16"; G-(INLET_RAD+1.5")=12"; H=3"; INLET_DIA=49 1/2"; INLET_RAD=24 3/4"; INLET_RAD+1.5"=26 1/4"; INLET_RAD/2=12 3/8"; J=3"; J*1.5=4 1/2"; J-.125"=2 7/8"; L=83 1/2"; M=11"; Model=CA-4 DWDI CW UBD Class 2; N=2 11/16"; N*2=5 3/8"; N+A+H=51 5/8"; N/2=1 11/32"; O=33 7/8"; P=67 3/4"; P/2=33 7/8"; S=24"; T=1 1/16"; T/2=17/32"
- 445_CA-4_DWDI_ARR_3_CW_UBD_CLASS_3: (B/2)+.125"=32 1/4"; (B/2)+J=35 1/8"; (F/2)-S=16 3/4"; -(B/2)-J=-35 1/8"; -A=-45 15/16"; -B=-64 1/4"; -B/2=-32 1/8"; -J*1.5=-4 1/2"; -L+M=-72 1/2"; A=45 15/16"; A+.25"=46 3/16"; B=64 1/4"; B+.25"=64 1/2"; B/2=32 1/8"; D=88 11/16"; D/2=44 11/32"; D/8=11 3/32"; E=37 1/8"; EE=37 1/8"; F=81 1/2"; F-G=43 1/4"; F/2=40 3/4"; G=38 1/4"; G+(INLET_RAD+1.5")=64 1/2"; G+N=41 3/16"; G-(INLET_RAD+1.5")=12"; H=3"; INLET_DIA=49 1/2"; INLET_RAD=24 3/4"; INLET_RAD+1.5"=26 1/4"; INLET_RAD/2=12 3/8"; J=3"; J*1.5=4 1/2"; J-.125"=2 7/8"; L=83 1/2"; M=11"; Model=CA-4 DWDI CW UBD Class 3; N=2 15/16"; N*2=5 7/8"; N+A+H=51 7/8"; N/2=1 15/32"; O=33 7/8"; P=67 3/4"; P/2=33 7/8"; S=24"; T=1 1/16"; T/2=17/32"
- 490_CA-4_DWDI_ARR_3_CW_UBD_CLASS_1: (B/2)+.125"=35 3/16"; (B/2)+J=38 1/16"; (F/2)-S=18 3/8"; -(B/2)-J=-38 1/16"; -A=-51"; -B=-70 1/8"; -B/2=-35 1/16"; -J*1.5=-4 1/2"; -L+M=-78"; A=51"; A+.25"=51 1/4"; B=70 1/8"; B+.25"=70 3/8"; B/2=35 1/16"; D=97 3/16"; D/2=48 19/32"; D/8=12 5/32"; E=40 3/4"; EE=40 3/4"; F=89 3/4"; F-G=47 1/2"; F/2=44 7/8"; G=42 1/4"; G+(INLET_RAD+1.5")=71 1/4"; G+N=45 3/16"; G-(INLET_RAD+1.5")=13 1/4"; H=3"; INLET_DIA=55"; INLET_RAD=27 1/2"; INLET_RAD+1.5"=29"; INLET_RAD/2=13 3/4"; J=3"; J*1.5=4 1/2"; J-.125"=2 7/8"; L=89 1/2"; M=11 1/2"; Model=CA-4 DWDI CW UBD Class 1; N=2 15/16"; N*2=5 7/8"; N+A+H=56 15/16"; N/2=1 15/32"; O=36 13/16"; P=73 5/8"; P/2=36 13/16"; S=26 1/2"; T=1 1/16"; T/2=17/32"
- 490_CA-4_DWDI_ARR_3_CW_UBD_CLASS_2: (B/2)+.125"=35 3/16"; (B/2)+J=38 1/16"; (F/2)-S=18 3/8"; -(B/2)-J=-38 1/16"; -A=-51"; -B=-70 1/8"; -B/2=-35 1/16"; -J*1.5=-4 1/2"; -L+M=-78 3/8"; A=51"; A+.25"=51 1/4"; B=70 1/8"; B+.25"=70 3/8"; B/2=35 1/16"; D=97 3/16"; D/2=48 19/32"; D/8=12 5/32"; E=40 3/4"; EE=40 3/4"; F=89 3/4"; F-G=47 1/2"; F/2=44 7/8"; G=42 1/4"; G+(INLET_RAD+1.5")=71 1/4"; G+N=45 11/16"; G-(INLET_RAD+1.5")=13 1/4"; H=3"; INLET_DIA=55"; INLET_RAD=27 1/2"; INLET_RAD+1.5"=29"; INLET_RAD/2=13 3/4"; J=3"; J*1.5=4 1/2"; J-.125"=2 7/8"; L=90 3/8"; M=12"; Model=CA-4 DWDI CW UBD Class 2; N=3 7/16"; N*2=6 7/8"; N+A+H=57 7/16"; N/2=1 23/32"; O=36 13/16"; P=73 5/8"; P/2=36 13/16"; S=26 1/2"; T=1 1/16"; T/2=17/32"
- 490_CA-4_DWDI_ARR_3_CW_UBD_CLASS_3: (B/2)+.125"=35 3/16"; (B/2)+J=38 1/16"; (F/2)-S=18 3/8"; -(B/2)-J=-38 1/16"; -A=-51"; -B=-70 1/8"; -B/2=-35 1/16"; -J*1.5=-4 1/2"; -L+M=-78 5/8"; A=51"; A+.25"=51 1/4"; B=70 1/8"; B+.25"=70 3/8"; B/2=35 1/16"; D=97 3/16"; D/2=48 19/32"; D/8=12 5/32"; E=40 3/4"; EE=40 3/4"; F=89 3/4"; F-G=47 1/2"; F/2=44 7/8"; G=42 1/4"; G+(INLET_RAD+1.5")=71 1/4"; G+N=45 11/16"; G-(INLET_RAD+1.5")=13 1/4"; H=3"; INLET_DIA=55"; INLET_RAD=27 1/2"; INLET_RAD+1.5"=29"; INLET_RAD/2=13 3/4"; J=3"; J*1.5=4 1/2"; J-.125"=2 7/8"; L=90 5/8"; M=12"; Model=CA-4 DWDI CW UBD Class 3; N=3 7/16"; N*2=6 7/8"; N+A+H=57 7/16"; N/2=1 23/32"; O=36 13/16"; P=73 5/8"; P/2=36 13/16"; S=26 1/2"; T=1 1/16"; T/2=17/32"
- 540_CA-4_DWDI_ARR_3_CW_UBD_CLASS_1: (B/2)+.125"=39 3/32"; (B/2)+J=41 31/32"; (F/2)-S=20 3/8"; -(B/2)-J=-41 31/32"; -A=-55 3/4"; -B=-77 15/16"; -B/2=-38 31/32"; -J*1.5=-4 1/2"; -L+M=-85 7/8"; A=55 3/4"; A+.25"=56"; B=77 15/16"; B+.25"=78 3/16"; B/2=38 31/32"; D=106 3/4"; D/2=53 3/8"; D/8=13 11/32"; E=44 7/8"; EE=44 7/8"; F=98 3/4"; F-G=52 1/4"; F/2=49 3/8"; G=46 1/2"; G+(INLET_RAD+1.5")=78"; G+N=49 15/16"; G-(INLET_RAD+1.5")=15"; H=3"; INLET_DIA=60"; INLET_RAD=30"; INLET_RAD+1.5"=31 1/2"; INLET_RAD/2=15"; J=3"; J*1.5=4 1/2"; J-.125"=2 7/8"; L=98 5/16"; M=12 7/16"; Model=CA-4 DWDI CW UBD Class 1; N=3 7/16"; N*2=6 7/8"; N+A+H=62 3/16"; N/2=1 23/32"; O=40 23/32"; P=81 7/16"; P/2=40 23/32"; S=29"; T=1 1/16"; T/2=17/32"
- 540_CA-4_DWDI_ARR_3_CW_UBD_CLASS_2: (B/2)+.125"=39 3/32"; (B/2)+J=41 31/32"; (F/2)-S=20 3/8"; -(B/2)-J=-41 31/32"; -A=-55 3/4"; -B=-77 15/16"; -B/2=-38 31/32"; -J*1.5=-4 1/2"; -L+M=-84 9/16"; A=55 3/4"; A+.25"=56"; B=77 15/16"; B+.25"=78 3/16"; B/2=38 31/32"; D=106 3/4"; D/2=53 3/8"; D/8=13 11/32"; E=44 7/8"; EE=44 7/8"; F=98 3/4"; F-G=52 1/4"; F/2=49 3/8"; G=46 1/2"; G+(INLET_RAD+1.5")=78"; G+N=50 7/16"; G-(INLET_RAD+1.5")=15"; H=3"; INLET_DIA=60"; INLET_RAD=30"; INLET_RAD+1.5"=31 1/2"; INLET_RAD/2=15"; J=3"; J*1.5=4 1/2"; J-.125"=2 7/8"; L=98 5/16"; M=13 3/4"; Model=CA-4 DWDI CW UBD Class 2; N=3 15/16"; N*2=7 7/8"; N+A+H=62 11/16"; N/2=1 31/32"; O=40 23/32"; P=81 7/16"; P/2=40 23/32"; S=29"; T=1 1/16"; T/2=17/32"
- 540_CA-4_DWDI_ARR_3_CW_UBD_CLASS_3: (B/2)+.125"=39 3/32"; (B/2)+J=41 31/32"; (F/2)-S=20 3/8"; -(B/2)-J=-41 31/32"; -A=-55 3/4"; -B=-77 15/16"; -B/2=-38 31/32"; -J*1.5=-4 1/2"; -L+M=-86"; A=55 3/4"; A+.25"=56"; B=77 15/16"; B+.25"=78 3/16"; B/2=38 31/32"; D=106 3/4"; D/2=53 3/8"; D/8=13 11/32"; E=44 7/8"; EE=44 7/8"; F=98 3/4"; F-G=52 1/4"; F/2=49 3/8"; G=46 1/2"; G+(INLET_RAD+1.5")=78"; G+N=50 7/16"; G-(INLET_RAD+1.5")=15"; H=3"; INLET_DIA=60"; INLET_RAD=30"; INLET_RAD+1.5"=31 1/2"; INLET_RAD/2=15"; J=3"; J*1.5=4 1/2"; J-.125"=2 7/8"; L=100 3/16"; M=14 3/16"; Model=CA-4 DWDI CW UBD Class 3; N=3 15/16"; N*2=7 7/8"; N+A+H=62 11/16"; N/2=1 31/32"; O=40 23/32"; P=81 7/16"; P/2=40 23/32"; S=29"; T=1 1/16"; T/2=17/32"
- 600_CA-4_DWDI_ARR_3_CW_UBD_CLASS_1: (B/2)+.125"=43 1/4"; (B/2)+J=46 1/8"; (F/2)-S=22 13/16"; -(B/2)-J=-46 1/8"; -A=-62 3/16"; -B=-86 1/4"; -B/2=-43 1/8"; -J*1.5=-4 1/2"; -L+M=-94 1/2"; A=62 3/16"; A+.25"=62 7/16"; B=86 1/4"; B+.25"=86 1/2"; B/2=43 1/8"; D=118 1/8"; D/2=59 1/16"; D/8=14 25/32"; E=49 3/4"; EE=49 3/4"; F=109 5/8"; F-G=58"; F/2=54 13/16"; G=51 5/8"; G+(INLET_RAD+1.5")=86 1/8"; G+N=55 1/16"; G-(INLET_RAD+1.5")=17 1/8"; H=3"; INLET_DIA=66"; INLET_RAD=33"; INLET_RAD+1.5"=34 1/2"; INLET_RAD/2=16 1/2"; J=3"; J*1.5=4 1/2"; J-.125"=2 7/8"; L=107 1/2"; M=13"; Model=CA-4 DWDI CW UBD Class 1; N=3 7/16"; N*2=6 7/8"; N+A+H=68 5/8"; N/2=1 23/32"; O=44 7/8"; P=89 3/4"; P/2=44 7/8"; S=32"; T=1 1/16"; T/2=17/32"
- 600_CA-4_DWDI_ARR_3_CW_UBD_CLASS_2: (B/2)+.125"=43 1/4"; (B/2)+J=46 1/8"; (F/2)-S=22 13/16"; -(B/2)-J=-46 1/8"; -A=-62 3/16"; -B=-86 1/4"; -B/2=-43 1/8"; -J*1.5=-4 1/2"; -L+M=-94 1/2"; A=62 3/16"; A+.25"=62 7/16"; B=86 1/4"; B+.25"=86 1/2"; B/2=43 1/8"; D=118 1/8"; D/2=59 1/16"; D/8=14 25/32"; E=49 3/4"; EE=49 3/4"; F=109 5/8"; F-G=58"; F/2=54 13/16"; G=51 5/8"; G+(INLET_RAD+1.5")=86 1/8"; G+N=55 9/16"; G-(INLET_RAD+1.5")=17 1/8"; H=3"; INLET_DIA=66"; INLET_RAD=33"; INLET_RAD+1.5"=34 1/2"; INLET_RAD/2=16 1/2"; J=3"; J*1.5=4 1/2"; J-.125"=2 7/8"; L=108 3/4"; M=14 1/4"; Model=CA-4 DWDI CW UBD Class 2; N=3 15/16"; N*2=7 7/8"; N+A+H=69 1/8"; N/2=1 31/32"; O=44 7/8"; P=89 3/4"; P/2=44 7/8"; S=32"; T=1 1/16"; T/2=17/32"
- 600_CA-4_DWDI_ARR_3_CW_UBD_CLASS_3: (B/2)+.125"=43 1/4"; (B/2)+J=46 1/8"; (F/2)-S=22 13/16"; -(B/2)-J=-46 1/8"; -A=-62 3/16"; -B=-86 1/4"; -B/2=-43 1/8"; -J*1.5=-4 1/2"; -L+M=-96"; A=62 3/16"; A+.25"=62 7/16"; B=86 1/4"; B+.25"=86 1/2"; B/2=43 1/8"; D=118 1/8"; D/2=59 1/16"; D/8=14 25/32"; E=49 3/4"; EE=49 3/4"; F=109 5/8"; F-G=58"; F/2=54 13/16"; G=51 5/8"; G+(INLET_RAD+1.5")=86 1/8"; G+N=56 1/16"; G-(INLET_RAD+1.5")=17 1/8"; H=3"; INLET_DIA=66"; INLET_RAD=33"; INLET_RAD+1.5"=34 1/2"; INLET_RAD/2=16 1/2"; J=3"; J*1.5=4 1/2"; J-.125"=2 7/8"; L=110 3/4"; M=14 3/4"; Model=CA-4 DWDI CW UBD Class 3; N=4 7/16"; N*2=8 7/8"; N+A+H=69 5/8"; N/2=2 7/32"; O=44 7/8"; P=89 3/4"; P/2=44 7/8"; S=32"; T=1 1/16"; T/2=17/32"

## geometry (parser evidence)
native form markers: Sweep x2
no freeform markers — native parametric forms only
